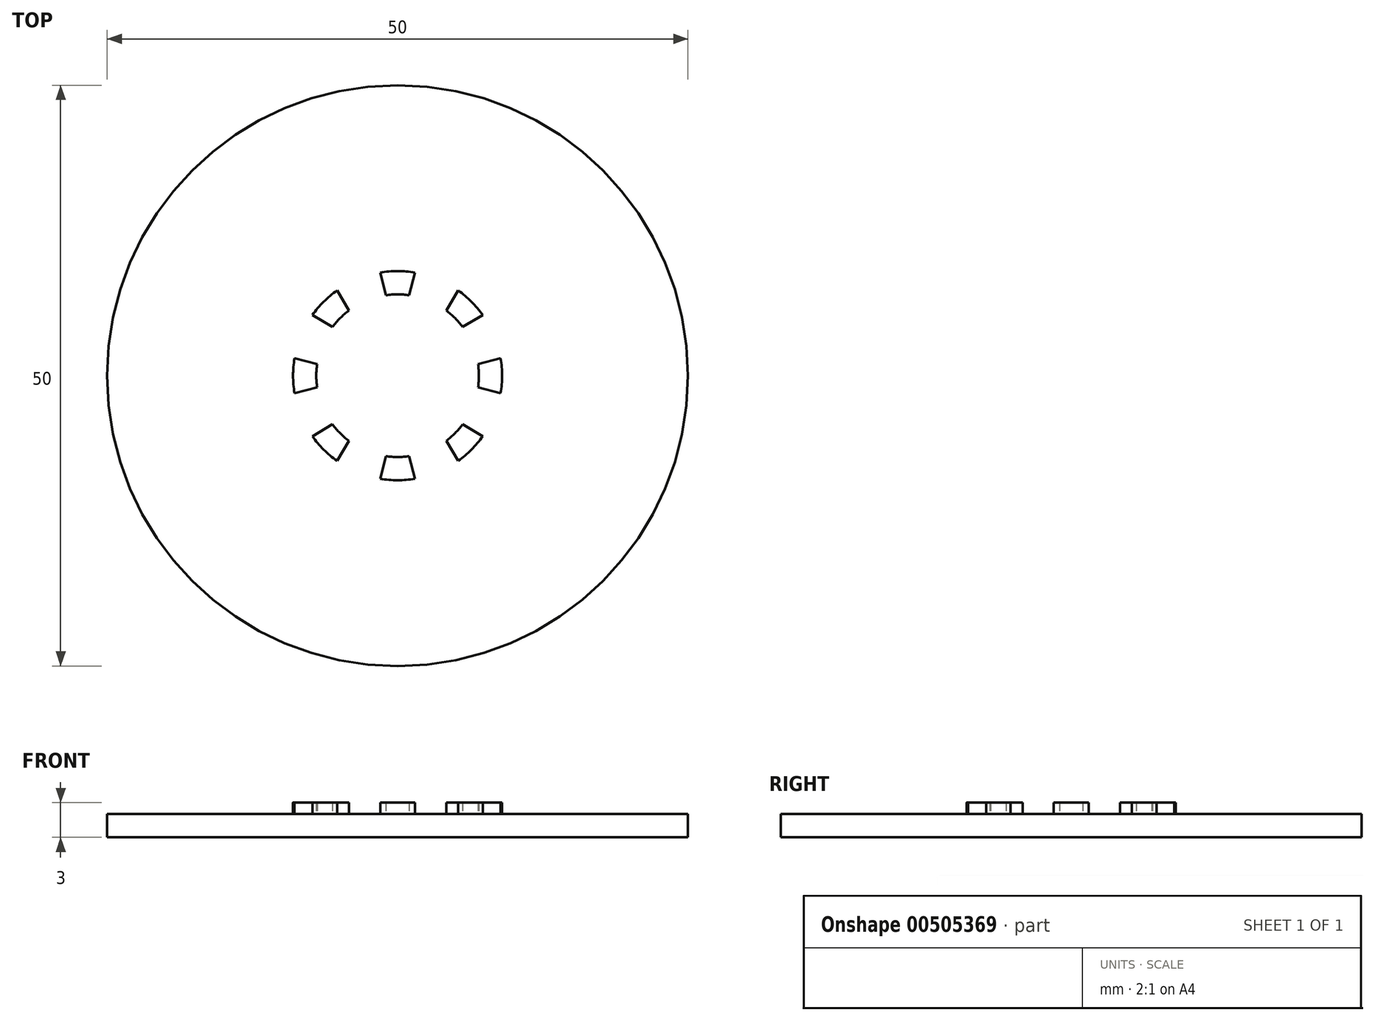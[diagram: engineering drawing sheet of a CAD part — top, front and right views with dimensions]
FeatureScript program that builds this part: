
annotation { "Feature Type Name" : "Feature", "Feature Type Description" : "" }
export const myFeature = defineFeature(function(context is Context, id is Id, definition is map)
    precondition{}
    {
        {
            var Q0;
            Q0=qCreatedBy(makeId("Top.planeOp"),FACE);
            var sketch = newSketch(context, id + "F0", { "sketchPlane" : qUnion([Q0])});
            skCircle(sketch, "E0", {"center": v(0, 0) * mm, "radius": 25 * mm});
            skSolve(sketch);
        }
        {
            var Q0;
            Q0 = qSketchRegion(id + "F0", true);
            extrude(context, id + "F1", {"entities" : qUnion([Q0]), "depth" : 2 * mm, "offsetDistance" : 25 * mm});
        }
        {
            var Q0;
            Q0=makeQuery(id+"F1.opExtrude","CAP_FACE",FACE,{"disambiguationData":[OSD([sQuery(id+"F0.wireOp",EDGE,"E0")])],"isStart":false});
            var sketch = newSketch(context, id + "F2", { "sketchPlane" : qUnion([Q0])});
            skCircle(sketch, "E1", {"center": v(0, 0) * mm, "radius": 9 * mm, "construction": true});
            skCircle(sketch, "E2", {"center": v(0, 0) * mm, "radius": 7 * mm, "construction": true});
            skLineSegment(sketch, "E3", {"start": v(-1.5, 8.87) * mm, "end": v(-1, 6.93) * mm});
            skArc(sketch, "E4", {"start": v(-1, 6.93) * mm, "mid": v(0, 7) * mm, "end": v(1, 6.93) * mm});
            skArc(sketch, "E5", {"start": v(-1.5, 8.87) * mm, "mid": v(0, 9) * mm, "end": v(1.5, 8.87) * mm});
            skLineSegment(sketch, "E6", {"start": v(1.5, 8.87) * mm, "end": v(1, 6.93) * mm});
            skSolve(sketch);
        }
        {
            var Q0;
            Q0=qCreatedBy(makeId("Right.planeOp"),FACE);
            var sketch = newSketch(context, id + "F3", { "sketchPlane" : qUnion([Q0])});
            skLineSegment(sketch, "E7", {"start": v(0, 0) * mm, "end": v(0, -27.9) * mm, "construction": true});
            skSolve(sketch);
        }
        {
            var Q0;
            Q0 = qSketchRegion(id + "F2", true);
            extrude(context, id + "F4", {"entities" : qUnion([Q0]), "depth" : 1 * mm, "offsetDistance" : 25 * mm});
        }
        {
            var Q0;
            Q0=makeQuery(id+"F4.opExtrude","SWEPT_BODY",BODY,{"disambiguationData":[OSD([sQuery(id+"F2.wireOp",EDGE,"E3"),sQuery(id+"F2.wireOp",EDGE,"E4"),sQuery(id+"F2.wireOp",EDGE,"E5"),sQuery(id+"F2.wireOp",EDGE,"E6")])]});
            var Q1;
            Q1=sQuery(id+"F3.wireOp",EDGE,"E7");
            circularPattern(context, id + "F5", {"entities" : qUnion([Q0]), "axis" : qUnion([Q1]), "angle" : 360 * degree, "instanceCount" : 8, "equalSpace" : true});
        }
    });
